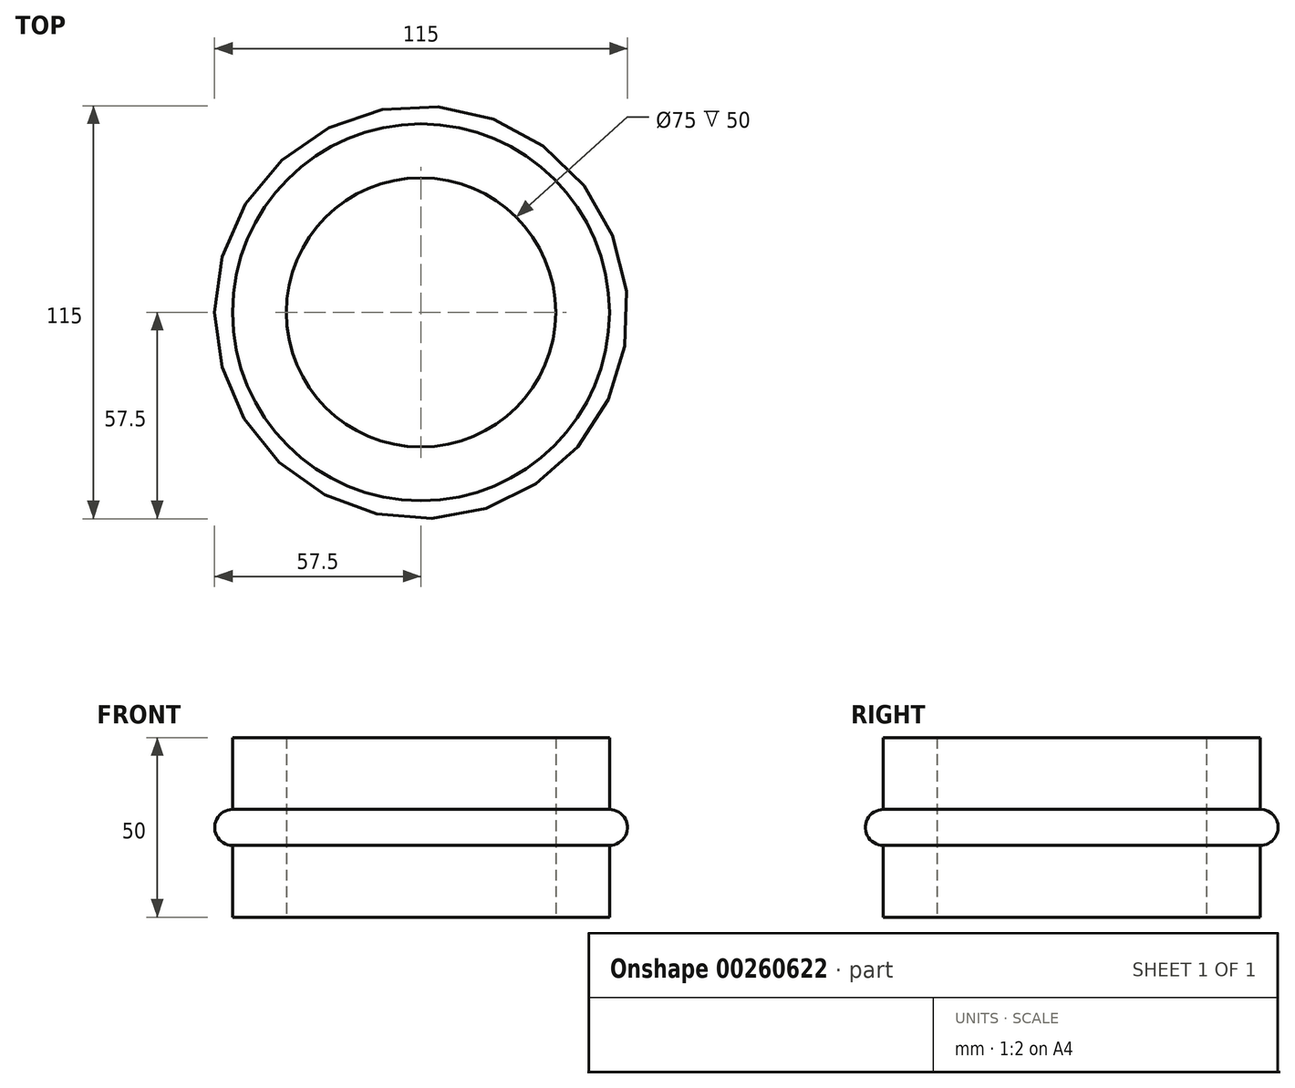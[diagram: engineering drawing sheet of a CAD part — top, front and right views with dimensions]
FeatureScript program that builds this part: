
annotation { "Feature Type Name" : "Feature", "Feature Type Description" : "" }
export const myFeature = defineFeature(function(context is Context, id is Id, definition is map)
    precondition{}
    {
        {
            var Q0;
            Q0=qCreatedBy(makeId("Front.planeOp"),FACE);
            var sketch = newSketch(context, id + "F0", { "sketchPlane" : qUnion([Q0])});
            skLineSegment(sketch, "E0", {"start": v(0, 0) * mm, "end": v(0, 50) * mm, "construction": true});
            skLineSegment(sketch, "E1.bottom", {"start": v(37.5, 0) * mm, "end": v(52.5, 0) * mm});
            skLineSegment(sketch, "E1.top", {"start": v(37.5, 50) * mm, "end": v(52.5, 50) * mm});
            skLineSegment(sketch, "E1.left", {"start": v(37.5, 0) * mm, "end": v(37.5, 50) * mm});
            skLineSegment(sketch, "E1.right", {"start": v(52.5, 0) * mm, "end": v(52.5, 50) * mm});
            skCircle(sketch, "E2", {"center": v(52.5, 25) * mm, "radius": 5 * mm});
            skSolve(sketch);
        }
        {
            var Q0;
            {var subQ1=sQuery(id+"F0.wireOp",EDGE,"E1.bottom");Q0=makeQuery(id+"F0.imprint","IMPRINT",FACE,{"disambiguationData":[TD([[makeQuery(id+"F0.imprint","IMPRINT",EDGE,{"derivedFrom":subQ1}),1.0]])]});}
            var Q1;
            {var subQ0=sQuery(id+"F0.wireOp",EDGE,"E2");var subQ1=sQuery(id+"F0.wireOp",EDGE,"E1.right");var subQ2=makeQuery(id+"F0.imprint","INTERSECT",VERTEX,{"disambiguationData":[OD(0.0)],"derivedFrom":[subQ1,subQ0]});Q1=makeQuery(id+"F0.imprint","IMPRINT",FACE,{"disambiguationData":[TD([[makeQuery(id+"F0.imprint","IMPRINT",EDGE,{"disambiguationData":[TD([[subQ2,-1.0]])],"derivedFrom":subQ1}),-1.0]])]});}
            var Q2;
            {var subQ0=sQuery(id+"F0.wireOp",EDGE,"E2");var subQ1=sQuery(id+"F0.wireOp",EDGE,"E1.right");var subQ2=makeQuery(id+"F0.imprint","INTERSECT",VERTEX,{"disambiguationData":[OD(0.0)],"derivedFrom":[subQ1,subQ0]});Q2=makeQuery(id+"F0.imprint","IMPRINT",FACE,{"disambiguationData":[TD([[makeQuery(id+"F0.imprint","IMPRINT",EDGE,{"disambiguationData":[TD([[subQ2,-1.0]])],"derivedFrom":subQ1}),1.0]])]});}
            var Q3;
            Q3=sQuery(id+"F0.wireOp",EDGE,"E0");
            revolve(context, id + "F1", {"entities" : qUnion([Q0, Q1, Q2]), "axis" : qUnion([Q3]), "revolveType" : RevolveType.FULL});
        }
    });
